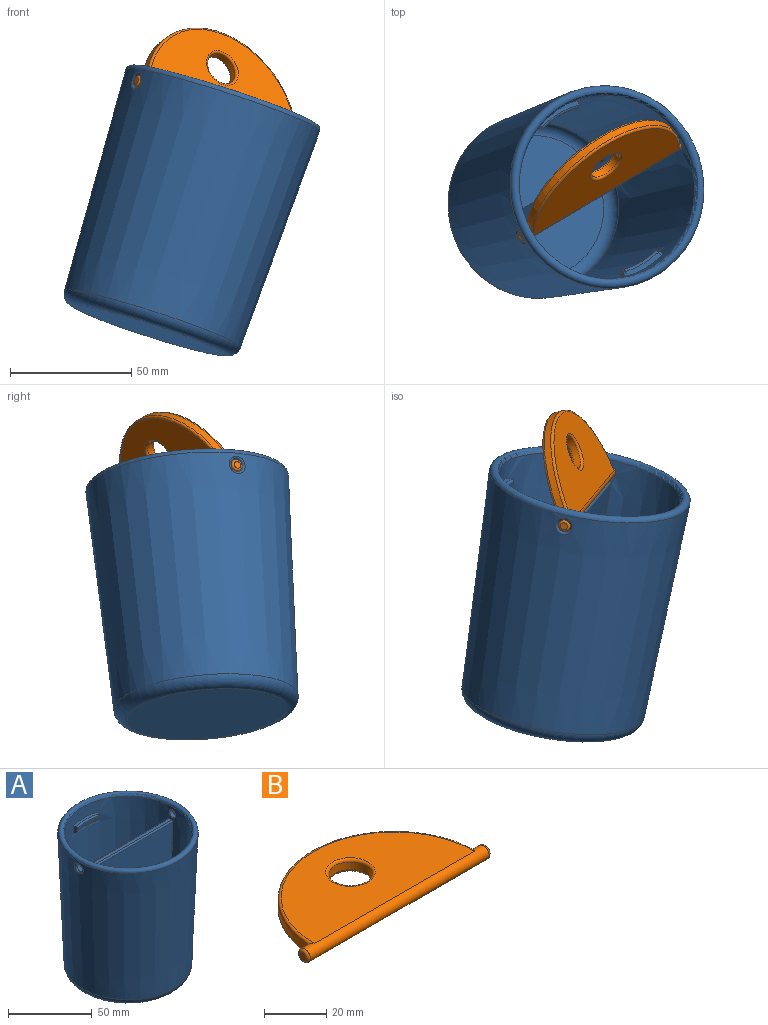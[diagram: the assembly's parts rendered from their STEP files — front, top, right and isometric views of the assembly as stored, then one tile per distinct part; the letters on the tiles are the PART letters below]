
ASSEMBLY  parts=2 mates=1
PART A: 60 faces, bbox 91.1x91.7x102.1 mm
  f0: cone r=38mm half-angle=2.3deg, axis (0,0,1), area 20040mm2, adj f2,f6,f7,f9,f10,f14,f15,f16
  f1: cone r=38.19mm half-angle=2.3deg, axis (0,0,1), area 23917.8mm2, adj f5,f6,f42,f43
  f2: torus R=29.35mm, axis (0,0,-1), area 749.8mm2, adj f0,f3,f15
  f3: plane 58.57x27.35mm, normal (0,0,1), area 1236.1mm2, adj f2,f15
  f4: plane 66.39x66.39mm, normal (0,0,-1), area 3462mm2, adj f5
  f5: torus R=33.2mm, axis (0,0,-1), area 1747.3mm2, adj f1,f4
  f6: torus R=40mm, axis (0,0,-1), area 1541.3mm2, adj f0,f1
  f7: torus R=29.35mm, axis (0,0,-1), area 749.8mm2, adj f0,f8,f14
  f8: plane 58.57x27.35mm, normal (0,0,1), area 1236.1mm2, adj f7,f14
  f9: plane 2x1mm, normal (0,0,1), area 2mm2, adj f0,f12,f50,f51
  f10: plane 2x1mm, normal (0,0,1), area 2mm2, adj f0,f13,f44,f45
  f11: plane 71.27x2mm, normal (0,0,1), area 142.5mm2, adj f48,f53,f56,f59
  f12: plane 28.96x2mm, normal (-1,0,-0.04), area 58mm2, adj f9,f54,f55,f59
  f13: plane 28.96x2mm, normal (1,0,-0.04), area 58mm2, adj f10,f46,f47,f48
  f14: plane 87.15x72.91mm, normal (0,-1,0), area 6109.7mm2, adj f0,f7,f8,f44,f46,f50,f53,f54
  f15: plane 87.15x72.91mm, normal (0,1,0), area 6109.7mm2, adj f0,f2,f3,f45,f47,f51,f55,f56
  f16: cylinder r=2.65mm len=5.3mm, axis (-1,0,0), area 50.1mm2, adj f0,f43
  f17: cylinder r=2.65mm len=5.3mm, axis (-1,0,0), area 50.7mm2, adj f0,f42
  f18: plane 17.56x2.97mm, normal (0,0,1), area 34.4mm2, adj f0,f22,f32,f37
  f19: cone r=34.94mm half-angle=42.7deg, axis (0,0,-1), area 62.5mm2, adj f0,f20,f36,f41
  f20: torus R=35.68mm, axis (0,0,-1), area 12.1mm2, adj f19,f21,f35,f40
  f21: cylinder r=34.68mm len=16.07mm, axis (0,0,-1), area 26.1mm2, adj f20,f22,f34,f39
  f22: torus R=35.68mm, axis (0,0,-1), area 25.7mm2, adj f18,f21,f33,f38
  f23: plane 3.59x1.91mm, normal (0.97,0.26,0), area 5mm2, adj f0,f37,f39,f41
  f24: plane 3.59x1.91mm, normal (-0.97,0.26,0), area 5mm2, adj f0,f32,f34,f36
  f25: torus R=35.68mm, axis (0,0,-1), area 28.8mm2, adj f26,f29,f30,f31
  f26: cylinder r=34.68mm len=17.95mm, axis (0,0,-1), area 29.2mm2, adj f25,f27,f30,f31
  f27: torus R=35.68mm, axis (0,0,-1), area 13.6mm2, adj f26,f28,f30,f31
  f28: cone r=34.94mm half-angle=42.7deg, axis (0,0,-1), area 69.7mm2, adj f0,f27,f30,f31
  f29: plane 19.5x3.22mm, normal (0,0,1), area 38.4mm2, adj f0,f25,f30,f31
  f30: plane 5.99x2.9mm, normal (-0.97,-0.26,0), area 12.9mm2, adj f0,f25,f26,f27,f28,f29
  f31: plane 5.99x2.9mm, normal (0.97,-0.26,0), area 12.9mm2, adj f0,f25,f26,f27,f28,f29
  f32: cylinder r=1mm len=2.19mm, axis (-0.26,-0.97,0), area 3.1mm2, adj f0,f18,f24,f33
  f33: sphere r=1mm, area 1mm2, adj f22,f32,f34
  f34: cylinder r=1mm len=1.61mm, axis (0,0,-1), area 2.5mm2, adj f21,f24,f33,f35
  f35: sphere r=1mm, area 0.7mm2, adj f20,f34,f36
  f36: bspline ~22.16x19.85mm, area 4.9mm2, adj f0,f19,f24,f35
  f37: cylinder r=1mm len=2.19mm, axis (-0.26,0.97,0), area 3.1mm2, adj f0,f18,f23,f38
  f38: sphere r=1mm, area 1mm2, adj f22,f37,f39
  f39: cylinder r=1mm len=1.61mm, axis (0,0,-1), area 2.5mm2, adj f21,f23,f38,f40
  f40: sphere r=1mm, area 0.7mm2, adj f20,f39,f41
  f41: bspline ~22.16x19.85mm, area 4.9mm2, adj f0,f19,f23,f40
  f42: bspline ~7.49x7.31mm, area 30.8mm2, adj f1,f17
  f43: bspline ~7.49x7.31mm, area 30.8mm2, adj f1,f16
  f44: cylinder r=1mm len=2.03mm, axis (1,0,0), area 2.3mm2, adj f0,f10,f14,f46
  f45: cylinder r=1mm len=2.03mm, axis (-1,0,0), area 2.3mm2, adj f0,f10,f15,f47
  f46: cylinder r=1mm len=30.04mm, axis (-0.04,0,-1), area 46.3mm2, adj f13,f14,f44,f49
  f47: cylinder r=1mm len=30.04mm, axis (0.04,0,1), area 46.3mm2, adj f13,f15,f45,f52
  f48: cylinder r=1mm len=2mm, axis (0,1,0), area 3.2mm2, adj f11,f13,f49,f52
  f49: sphere r=1mm, area 1.6mm2, adj f46,f48,f53
  f50: cylinder r=1mm len=2.03mm, axis (1,0,0), area 2.3mm2, adj f0,f9,f14,f54
  f51: cylinder r=1mm len=2.03mm, axis (-1,0,0), area 2.3mm2, adj f0,f9,f15,f55
  f52: sphere r=1mm, area 1.6mm2, adj f47,f48,f56
  f53: cylinder r=1mm len=71.27mm, axis (1,0,0), area 112mm2, adj f11,f14,f49,f57
  f54: cylinder r=1mm len=30.04mm, axis (-0.04,0,1), area 46.3mm2, adj f12,f14,f50,f57
  f55: cylinder r=1mm len=30.04mm, axis (0.04,0,-1), area 46.3mm2, adj f12,f15,f51,f58
  f56: cylinder r=1mm len=71.27mm, axis (-1,0,0), area 112mm2, adj f11,f15,f52,f58
  f57: sphere r=1mm, area 2.2mm2, adj f53,f54,f59
  f58: sphere r=1mm, area 2.2mm2, adj f55,f56,f59
  f59: cylinder r=1mm len=2mm, axis (0,-1,0), area 3.2mm2, adj f11,f12,f57,f58
PART B: 13 faces, bbox 83.5x43.3x5.4 mm
  f0: cylinder r=2.5mm len=81.5mm, axis (-1,0,0), area 695.3mm2, adj f3,f4,f5,f9,f10,f11,f12
  f1: plane 3x3mm, normal (1,0,0), area 7.1mm2, adj f12
  f2: plane 3x3mm, normal (-1,0,0), area 7.1mm2, adj f11
  f3: cylinder r=37.5mm len=74.89mm, axis (0,0,-1), area 339.3mm2, adj f0,f9,f10
  f4: plane 72.99x36.5mm, normal (0,0,1), area 1891.3mm2, adj f0,f8,f10
  f5: plane 72.99x36.5mm, normal (0,0,-1), area 1891.3mm2, adj f0,f7,f9
  f6: cylinder r=7mm len=14mm, axis (0,0,1), area 131.9mm2, adj f7,f8
  f7: torus R=8mm, axis (0,0,1), area 72.7mm2, adj f5,f6
  f8: torus R=8mm, axis (0,0,1), area 72.7mm2, adj f4,f6
  f9: torus R=36.5mm, axis (0,0,1), area 179.7mm2, adj f0,f3,f5
  f10: torus R=36.5mm, axis (0,0,1), area 179.7mm2, adj f0,f3,f4
  f11: torus R=1.5mm, axis (1,0,0), area 21.1mm2, adj f0,f2
  f12: torus R=1.5mm, axis (1,0,0), area 21.1mm2, adj f0,f1
PLACE A rot(axis=(0,0.53,0.85),35deg) t=(-60.1,48.9,-24.49)mm
PLACE B rot(axis=(0.84,0.48,0.26),66.8deg) t=(-85.71,122.49,24.32)mm
MATE cylindrical B.f0 <-> A.f16  axis (-0.82,-0.49,0.3) through (-31.22,56.58,65.69)mm
